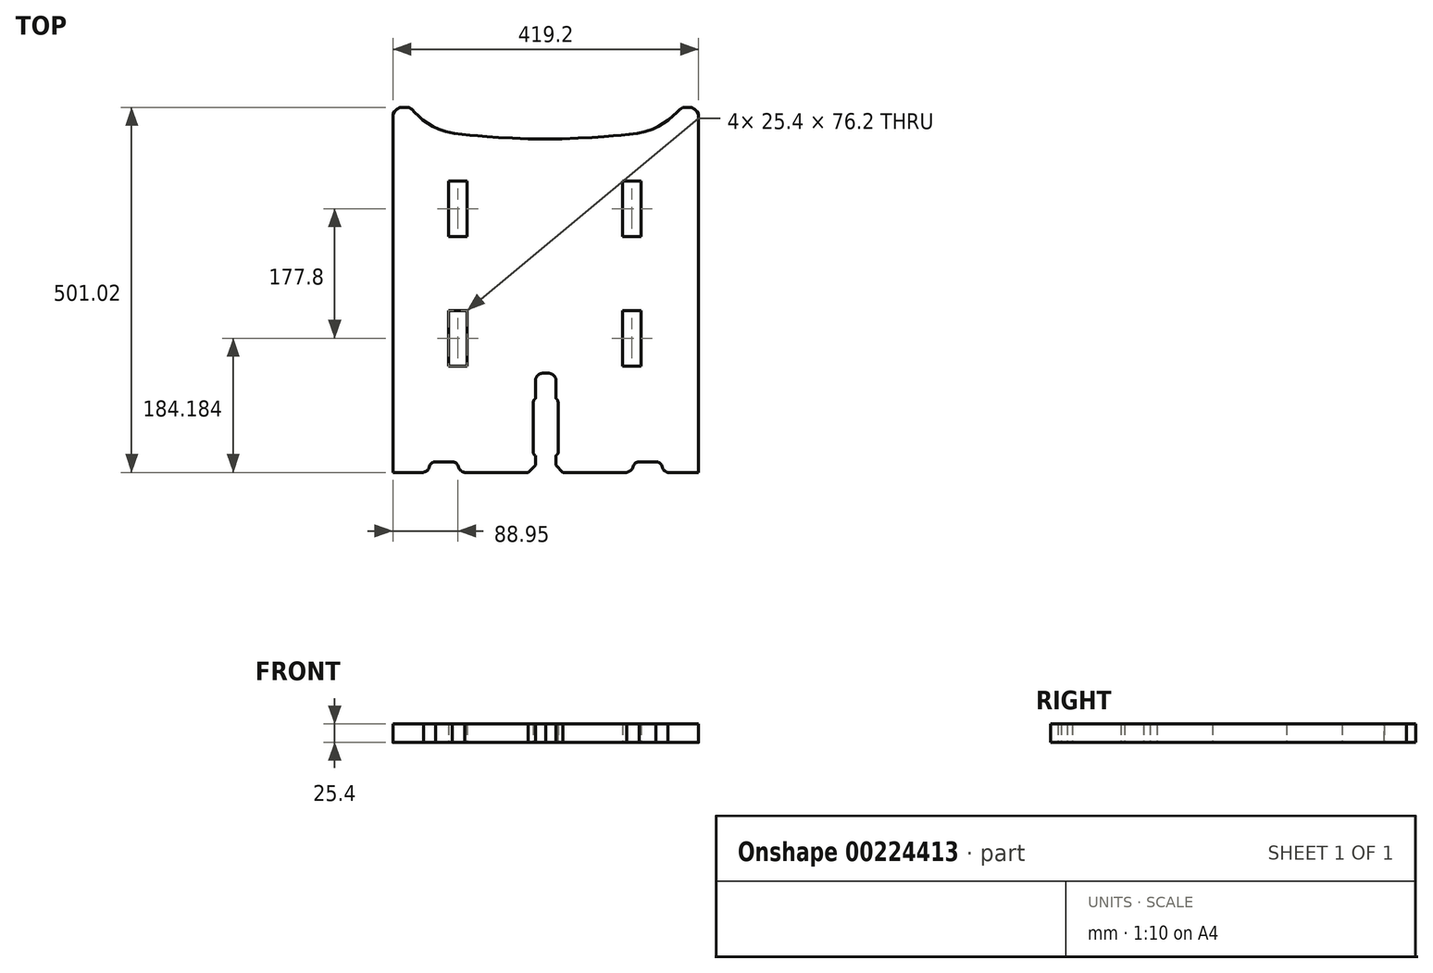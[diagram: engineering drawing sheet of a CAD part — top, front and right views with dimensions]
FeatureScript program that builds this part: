
annotation { "Feature Type Name" : "Feature", "Feature Type Description" : "" }
export const myFeature = defineFeature(function(context is Context, id is Id, definition is map)
    precondition{}
    {
        {
            var Q0;
            Q0=qCreatedBy(makeId("Top.planeOp"),FACE);
            var sketch = newSketch(context, id + "F0", { "sketchPlane" : qUnion([Q0])});
            skLineSegment(sketch, "E0", {"start": v(27.94, 9.6) * mm, "end": v(69.8, 9.6) * mm});
            skLineSegment(sketch, "E1", {"start": v(27.94, 9.6) * mm, "end": v(27.94, 497.74) * mm});
            skLineSegment(sketch, "E2", {"start": v(27.94, 497.74) * mm, "end": v(27.94, 9.6) * mm});
            skFitSpline(sketch, "E3", {"points": [v(27.94, 497.74) * mm, v(27.94, 500.26) * mm, v(28.58, 502.83) * mm, v(29.68, 504.7) * mm, v(31.15, 506.24) * mm, v(33.73, 508.55) * mm, v(37.58, 510.16) * mm, v(42.14, 510.54) * mm, v(48.7, 510.35) * mm, v(53.07, 508.49) * mm, v(56.41, 505.15) * mm, v(60.72, 501.03) * mm, v(67.92, 494.03) * mm, v(76.98, 488.18) * mm, v(86.17, 482.65) * mm, v(101.02, 477.27) * mm, v(121.29, 473.63) * mm, v(139.73, 472.06) * mm, v(167.51, 469.63) * mm, v(236.38, 467.37) * mm], "startDerivative": vector(-4.81, 90.89) * mm, "endDerivative": vector(535.6, 1.58) * mm});
            skFitSpline(sketch, "E4", {"points": [v(69.8, 9.6) * mm, v(73.23, 11.19) * mm, v(75.8, 13.3) * mm, v(77.23, 16.34) * mm, v(78.38, 19.6) * mm, v(80.27, 21.95) * mm, v(83.2, 23.84) * mm, v(86.11, 24.07) * mm], "startDerivative": vector(23.27, 9.7) * mm, "endDerivative": vector(21.94, -0.97) * mm});
            skLineSegment(sketch, "E5", {"start": v(86.11, 24.07) * mm, "end": v(109.01, 24.07) * mm});
            skFitSpline(sketch, "E6", {"points": [v(109.01, 24.07) * mm, v(112.2, 23.57) * mm, v(114.92, 22) * mm, v(116.86, 19.45) * mm, v(117.83, 16.78) * mm, v(119.17, 14.23) * mm, v(121.05, 12.1) * mm, v(123.66, 10.47) * mm, v(126.39, 9.6) * mm], "startDerivative": vector(25.16, -2.06) * mm, "endDerivative": vector(22.52, -5.95) * mm});
            skLineSegment(sketch, "E7.trimOffspring", {"start": v(126.39, 9.6) * mm, "end": v(213.7, 9.6) * mm});
            skLineSegment(sketch, "E8", {"start": v(213.7, 9.6) * mm, "end": v(223.6, 19.64) * mm});
            skLineSegment(sketch, "E9", {"start": v(223.6, 19.64) * mm, "end": v(223.6, 32.64) * mm});
            skFitSpline(sketch, "E10", {"points": [v(223.6, 32.64) * mm, v(222.44, 33.51) * mm, v(220.8, 35.44) * mm, v(220.42, 39.39) * mm], "startDerivative": vector(-4.32, 3.1) * mm, "endDerivative": vector(0.29, 10.38) * mm});
            skLineSegment(sketch, "E11", {"start": v(220.42, 39.39) * mm, "end": v(220.42, 106.01) * mm});
            skFitSpline(sketch, "E12", {"points": [v(220.42, 106.01) * mm, v(221.43, 109.1) * mm, v(223.48, 111.16) * mm], "startDerivative": vector(1.38, 6.46) * mm, "endDerivative": vector(4.78, 3.8) * mm});
            skLineSegment(sketch, "E13", {"start": v(223.48, 111.16) * mm, "end": v(223.48, 137.55) * mm});
            skFitSpline(sketch, "E14", {"points": [v(223.48, 137.55) * mm, v(225.03, 140.99) * mm, v(228.23, 144.08) * mm, v(232.24, 145.68) * mm, v(237.5, 145.91) * mm], "startDerivative": vector(5.32, 15.26) * mm, "endDerivative": vector(20, -0.36) * mm});
            skFitSpline(sketch, "E15.MirrorCS", {"points": [v(251.38, 32.64) * mm, v(252.54, 33.51) * mm, v(254.18, 35.44) * mm, v(254.56, 39.39) * mm], "startDerivative": vector(4.32, 3.1) * mm, "endDerivative": vector(-0.29, 10.38) * mm});
            skFitSpline(sketch, "E16.MirrorCS", {"points": [v(254.56, 106.01) * mm, v(253.55, 109.1) * mm, v(251.5, 111.16) * mm], "startDerivative": vector(-1.38, 6.46) * mm, "endDerivative": vector(-4.78, 3.8) * mm});
            skFitSpline(sketch, "E17.MirrorCS", {"points": [v(405.19, 9.6) * mm, v(401.75, 11.19) * mm, v(399.18, 13.3) * mm, v(397.75, 16.34) * mm, v(396.6, 19.6) * mm, v(394.71, 21.95) * mm, v(391.79, 23.84) * mm, v(388.87, 24.07) * mm], "startDerivative": vector(-23.27, 9.7) * mm, "endDerivative": vector(-21.94, -0.97) * mm});
            skLineSegment(sketch, "E18.MirrorCS", {"start": v(388.87, 24.07) * mm, "end": v(365.97, 24.07) * mm});
            skFitSpline(sketch, "E19.MirrorCS", {"points": [v(365.97, 24.07) * mm, v(362.79, 23.57) * mm, v(360.06, 22) * mm, v(358.12, 19.45) * mm, v(357.15, 16.78) * mm, v(355.81, 14.23) * mm, v(353.93, 12.1) * mm, v(351.32, 10.47) * mm, v(348.6, 9.6) * mm], "startDerivative": vector(-25.16, -2.06) * mm, "endDerivative": vector(-22.52, -5.95) * mm});
            skLineSegment(sketch, "E20.MirrorCS", {"start": v(251.38, 19.64) * mm, "end": v(251.38, 32.64) * mm});
            skFitSpline(sketch, "E21.MirrorCS", {"points": [v(251.5, 137.55) * mm, v(249.95, 140.99) * mm, v(246.75, 144.08) * mm, v(242.74, 145.68) * mm, v(237.5, 145.91) * mm], "startDerivative": vector(-5.32, 15.26) * mm, "endDerivative": vector(-20, -0.36) * mm});
            skLineSegment(sketch, "E22.MirrorCS", {"start": v(261.29, 9.6) * mm, "end": v(251.38, 19.64) * mm});
            skLineSegment(sketch, "E23.MirrorCS", {"start": v(447.04, 9.6) * mm, "end": v(447.04, 497.74) * mm});
            skLineSegment(sketch, "E24.MirrorCS", {"start": v(251.5, 111.16) * mm, "end": v(251.5, 137.55) * mm});
            skFitSpline(sketch, "E25.MirrorCS", {"points": [v(447.04, 497.74) * mm, v(447.04, 500.26) * mm, v(446.4, 502.83) * mm, v(445.3, 504.7) * mm, v(443.83, 506.24) * mm, v(441.25, 508.55) * mm, v(437.4, 510.16) * mm, v(432.84, 510.54) * mm, v(426.28, 510.35) * mm, v(421.9, 508.49) * mm, v(418.57, 505.15) * mm, v(414.26, 501.03) * mm, v(407.06, 494.03) * mm, v(398, 488.18) * mm, v(388.8, 482.65) * mm, v(373.96, 477.27) * mm, v(353.7, 473.63) * mm, v(335.25, 472.06) * mm, v(307.47, 469.63) * mm, v(236.38, 467.37) * mm], "startDerivative": vector(4.81, 90.89) * mm, "endDerivative": vector(-535.6, 1.58) * mm});
            skLineSegment(sketch, "E26.MirrorCS", {"start": v(254.56, 39.39) * mm, "end": v(254.56, 106.01) * mm});
            skLineSegment(sketch, "E27.MirrorCS", {"start": v(447.04, 9.6) * mm, "end": v(405.19, 9.6) * mm});
            skLineSegment(sketch, "E28.MirrorCS", {"start": v(348.6, 9.6) * mm, "end": v(261.29, 9.6) * mm});
            skLineSegment(sketch, "E29.MirrorCS", {"start": v(447.04, 497.74) * mm, "end": v(447.04, 9.6) * mm});
            skLineSegment(sketch, "E30.bottom", {"start": v(129.54, 333.47) * mm, "end": v(104.14, 333.47) * mm});
            skLineSegment(sketch, "E30.top", {"start": v(129.54, 409.67) * mm, "end": v(104.14, 409.67) * mm});
            skLineSegment(sketch, "E30.left", {"start": v(129.54, 333.47) * mm, "end": v(129.54, 409.67) * mm});
            skLineSegment(sketch, "E30.right", {"start": v(104.14, 333.47) * mm, "end": v(104.14, 409.67) * mm});
            skPoint(sketch, "E30.middle", {"position": v(116.84, 371.57) * mm});
            skLineSegment(sketch, "E31.bottom", {"start": v(129.54, 231.87) * mm, "end": v(104.14, 231.87) * mm});
            skLineSegment(sketch, "E31.top", {"start": v(129.54, 155.67) * mm, "end": v(104.14, 155.67) * mm});
            skLineSegment(sketch, "E31.left", {"start": v(129.54, 231.87) * mm, "end": v(129.54, 155.67) * mm});
            skLineSegment(sketch, "E31.right", {"start": v(104.14, 231.87) * mm, "end": v(104.14, 155.67) * mm});
            skPoint(sketch, "E31.middle", {"position": v(116.84, 193.77) * mm});
            skPoint(sketch, "E31.middle.positionSnap0", {"position": v(116.84, 333.47) * mm});
            skPoint(sketch, "E31.centerSnap0", {"position": v(116.84, 333.47) * mm});
            skLineSegment(sketch, "E32.MirrorCS", {"start": v(343.21, 333.47) * mm, "end": v(368.61, 333.47) * mm});
            skPoint(sketch, "E33.MirrorP", {"position": v(355.91, 333.47) * mm});
            skLineSegment(sketch, "E34.MirrorCS", {"start": v(343.21, 333.47) * mm, "end": v(343.21, 409.67) * mm});
            skPoint(sketch, "E35.MirrorP", {"position": v(355.91, 371.57) * mm});
            skLineSegment(sketch, "E36.MirrorCS", {"start": v(343.21, 409.67) * mm, "end": v(368.61, 409.67) * mm});
            skLineSegment(sketch, "E37.MirrorCS", {"start": v(368.61, 231.87) * mm, "end": v(368.61, 155.67) * mm});
            skLineSegment(sketch, "E38.MirrorCS", {"start": v(343.21, 231.87) * mm, "end": v(343.21, 155.67) * mm});
            skLineSegment(sketch, "E39.MirrorCS", {"start": v(343.21, 155.67) * mm, "end": v(368.61, 155.67) * mm});
            skLineSegment(sketch, "E40.MirrorCS", {"start": v(343.21, 231.87) * mm, "end": v(368.61, 231.87) * mm});
            skPoint(sketch, "E41.MirrorP", {"position": v(355.91, 193.77) * mm});
            skLineSegment(sketch, "E42.MirrorCS", {"start": v(368.61, 333.47) * mm, "end": v(368.61, 409.67) * mm});
            skSolve(sketch);
        }
        {
            var Q0;
            Q0 = qSketchRegion(id + "F0", true);
            extrude(context, id + "F1", {"entities" : qUnion([Q0]), "depth" : 25.4 * mm});
        }
    });
